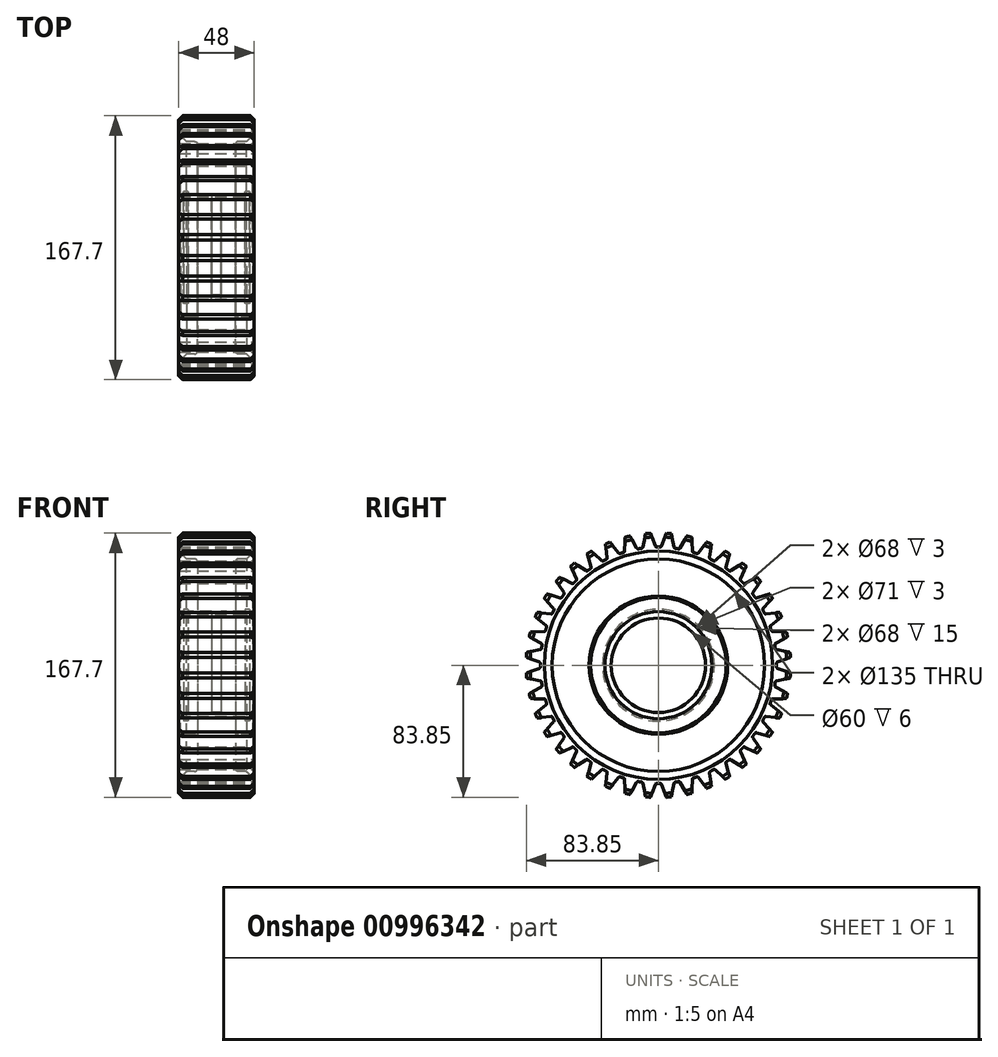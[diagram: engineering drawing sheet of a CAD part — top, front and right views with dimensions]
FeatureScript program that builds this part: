
annotation { "Feature Type Name" : "Feature", "Feature Type Description" : "" }
export const myFeature = defineFeature(function(context is Context, id is Id, definition is map)
    precondition{}
    {
        {
            var Q0;
            Q0=qCreatedBy(makeId("Front.planeOp"),FACE);
            var sketch = newSketch(context, id + "F0", { "sketchPlane" : qUnion([Q0])});
            skLineSegment(sketch, "E0", {"start": v(0, 0) * mm, "end": v(0, 84) * mm, "construction": true});
            skLineSegment(sketch, "E1", {"start": v(0, 84) * mm, "end": v(-24, 84) * mm});
            skLineSegment(sketch, "E2", {"start": v(-24, 84) * mm, "end": v(-24, 67.5) * mm});
            skLineSegment(sketch, "E3", {"start": v(-24, 0) * mm, "end": v(0, 0) * mm, "construction": true});
            skLineSegment(sketch, "E4", {"start": v(-24, 34) * mm, "end": v(-21, 34) * mm});
            skLineSegment(sketch, "E5", {"start": v(-21, 34) * mm, "end": v(-21, 35.5) * mm});
            skLineSegment(sketch, "E6", {"start": v(-21, 35.5) * mm, "end": v(-18, 35.5) * mm});
            skLineSegment(sketch, "E7", {"start": v(-18, 35.5) * mm, "end": v(-18, 34) * mm});
            skLineSegment(sketch, "E8", {"start": v(-18, 34) * mm, "end": v(-3, 34) * mm});
            skLineSegment(sketch, "E9", {"start": v(-3, 34) * mm, "end": v(-3, 30) * mm});
            skLineSegment(sketch, "E10", {"start": v(-3, 30) * mm, "end": v(0, 30) * mm});
            skLineSegment(sketch, "E11", {"start": v(-24, 44) * mm, "end": v(-14, 44) * mm});
            skLineSegment(sketch, "E12", {"start": v(-12, 46) * mm, "end": v(-12, 65.5) * mm});
            skLineSegment(sketch, "E13", {"start": v(-14, 67.5) * mm, "end": v(-24, 67.5) * mm});
            skLineSegment(sketch, "E14.trimOffspring", {"start": v(-24, 44) * mm, "end": v(-24, 34) * mm});
            skPoint(sketch, "E15.visualSharp", {"position": v(-12, 67.5) * mm});
            skArc(sketch, "E15.filletArc", {"start": v(-12, 65.5) * mm, "mid": v(-12.59, 66.91) * mm, "end": v(-14, 67.5) * mm});
            skPoint(sketch, "E16.visualSharp", {"position": v(-12, 44) * mm});
            skArc(sketch, "E16.filletArc", {"start": v(-14, 44) * mm, "mid": v(-12.59, 44.59) * mm, "end": v(-12, 46) * mm});
            skLineSegment(sketch, "E17.MirrorCS", {"start": v(0, 84) * mm, "end": v(24, 84) * mm});
            skLineSegment(sketch, "E18.MirrorCS", {"start": v(24, 84) * mm, "end": v(24, 67.5) * mm});
            skLineSegment(sketch, "E19.MirrorCS", {"start": v(14, 67.5) * mm, "end": v(24, 67.5) * mm});
            skArc(sketch, "E20.MirrorCS", {"start": v(12, 65.5) * mm, "mid": v(12.59, 66.91) * mm, "end": v(14, 67.5) * mm});
            skLineSegment(sketch, "E21.MirrorCS", {"start": v(12, 46) * mm, "end": v(12, 65.5) * mm});
            skArc(sketch, "E22.MirrorCS", {"start": v(14, 44) * mm, "mid": v(12.59, 44.59) * mm, "end": v(12, 46) * mm});
            skLineSegment(sketch, "E23.MirrorCS", {"start": v(24, 44) * mm, "end": v(14, 44) * mm});
            skLineSegment(sketch, "E24.MirrorCS", {"start": v(24, 44) * mm, "end": v(24, 34) * mm});
            skLineSegment(sketch, "E25.MirrorCS", {"start": v(24, 34) * mm, "end": v(21, 34) * mm});
            skLineSegment(sketch, "E26.MirrorCS", {"start": v(21, 34) * mm, "end": v(21, 35.5) * mm});
            skLineSegment(sketch, "E27.MirrorCS", {"start": v(21, 35.5) * mm, "end": v(18, 35.5) * mm});
            skLineSegment(sketch, "E28.MirrorCS", {"start": v(18, 35.5) * mm, "end": v(18, 34) * mm});
            skLineSegment(sketch, "E29.MirrorCS", {"start": v(18, 34) * mm, "end": v(3, 34) * mm});
            skLineSegment(sketch, "E30.MirrorCS", {"start": v(3, 34) * mm, "end": v(3, 30) * mm});
            skLineSegment(sketch, "E31.MirrorCS", {"start": v(3, 30) * mm, "end": v(0, 30) * mm});
            skSolve(sketch);
        }
        {
            var Q0;
            Q0=makeQuery(id+"F0.imprint","IMPRINT",FACE,{"disambiguationData":[TD([[makeQuery(id+"F0.imprint","IMPRINT",EDGE,{"derivedFrom":sQuery(id+"F0.wireOp",EDGE,"E1")}),1.0]])]});
            var Q1;
            Q1=sQuery(id+"F0.wireOp",EDGE,"E3");
            revolve(context, id + "F1", {"surfaceOperationType" : NewSurfaceOperationType.NEW, "entities" : qUnion([Q0]), "axis" : qUnion([Q1]), "revolveType" : RevolveType.FULL});
        }
        {
            var Q0;
            Q0=qCreatedBy(makeId("Right.planeOp"),FACE);
            var sketch = newSketch(context, id + "F2", { "sketchPlane" : qUnion([Q0])});
            skLineSegment(sketch, "E32", {"start": v(0, 0) * mm, "end": v(0, 100.92) * mm, "construction": true});
            skArc(sketch, "E33", {"start": v(1.04, 75) * mm, "mid": v(0, 75) * mm, "end": v(-1.04, 75) * mm});
            skLineSegment(sketch, "E34", {"start": v(2, 75.65) * mm, "end": v(4.98, 83.85) * mm});
            skLineSegment(sketch, "E35.MirrorCS", {"start": v(-2, 75.65) * mm, "end": v(-4.98, 83.85) * mm});
            skPoint(sketch, "E36.visualSharp", {"position": v(-1.75, 74.98) * mm});
            skArc(sketch, "E36.filletArc", {"start": v(-2, 75.65) * mm, "mid": v(-1.62, 75.17) * mm, "end": v(-1.04, 75) * mm});
            skPoint(sketch, "E37.visualSharp", {"position": v(1.75, 74.98) * mm});
            skArc(sketch, "E37.filletArc", {"start": v(1.04, 75) * mm, "mid": v(1.62, 75.17) * mm, "end": v(2, 75.65) * mm});
            skArc(sketch, "E38", {"start": v(-4.98, 83.85) * mm, "mid": v(0, 84) * mm, "end": v(4.98, 83.85) * mm});
            skSolve(sketch);
        }
        {
            var Q0;
            Q0 = qSketchRegion(id + "F2", true);
            extrude(context, id + "F3", {"entities" : qUnion([Q0]), "operationType" : NewBodyOperationType.REMOVE, "endBound" : BoundingType.SYMMETRIC, "oppositeDirection" : true, "depth" : 50 * mm, "offsetDistance" : 25 * mm});
        }
        {
            var Q0;
            Q0=makeQuery(id+"F3.boolean.opBoolean","COPY",FACE,{"derivedFrom":makeQuery(id+"F3.opExtrude","SWEPT_FACE",FACE,{"disambiguationData":[OSD([sQuery(id+"F2.wireOp",EDGE,"E35.MirrorCS")])]})});
            var Q1;
            Q1=makeQuery(id+"F3.boolean.opBoolean","COPY",FACE,{"derivedFrom":makeQuery(id+"F3.opExtrude","SWEPT_FACE",FACE,{"disambiguationData":[OSD([sQuery(id+"F2.wireOp",EDGE,"E36.filletArc")])]})});
            var Q2;
            Q2=makeQuery(id+"F3.boolean.opBoolean","COPY",FACE,{"derivedFrom":makeQuery(id+"F3.opExtrude","SWEPT_FACE",FACE,{"disambiguationData":[OSD([sQuery(id+"F2.wireOp",EDGE,"E33")])]})});
            var Q3;
            Q3=makeQuery(id+"F3.boolean.opBoolean","COPY",FACE,{"derivedFrom":makeQuery(id+"F3.opExtrude","SWEPT_FACE",FACE,{"disambiguationData":[OSD([sQuery(id+"F2.wireOp",EDGE,"E37.filletArc")])]})});
            var Q4;
            Q4=makeQuery(id+"F3.boolean.opBoolean","COPY",FACE,{"derivedFrom":makeQuery(id+"F3.opExtrude","SWEPT_FACE",FACE,{"disambiguationData":[OSD([sQuery(id+"F2.wireOp",EDGE,"E34")])]})});
            var Q5;
            Q5=makeQuery(id+"F1.opRevolve","SWEPT_FACE",FACE,{"disambiguationData":[OSD([sQuery(id+"F0.wireOp",EDGE,"E1"),sQuery(id+"F0.wireOp",EDGE,"E17.MirrorCS")])]});
            circularPattern(context, id + "F4", {"patternType" : PatternType.FACE, "operationType" : NewBodyOperationType.REMOVE, "faces" : qUnion([Q0, Q1, Q2, Q3, Q4]), "axis" : qUnion([Q5]), "angle" : 9 * degree, "instanceCount" : 40});
        }
        {
            var Q0;
            Q0=makeQuery(id+"F1.opRevolve","SWEPT_EDGE",EDGE,{"disambiguationData":[OSD([sQuery(id+"F0.wireOp",EDGE,"E18.MirrorCS"),sQuery(id+"F0.wireOp",EDGE,"E19.MirrorCS")])]});
            var Q1;
            Q1=makeQuery(id+"F1.opRevolve","SWEPT_EDGE",EDGE,{"disambiguationData":[OSD([sQuery(id+"F0.wireOp",EDGE,"E2"),sQuery(id+"F0.wireOp",EDGE,"E13")])]});
            chamfer(context, id + "F5", {"entities" : qUnion([Q0, Q1]), "width" : 5 * mm, "tangentPropagation" : true});
        }
        {
            var Q0;
            Q0=makeQuery(id+"F1.opRevolve","SWEPT_EDGE",EDGE,{"disambiguationData":[OSD([sQuery(id+"F0.wireOp",EDGE,"E11"),sQuery(id+"F0.wireOp",EDGE,"E14.trimOffspring")])]});
            var Q1;
            Q1=makeQuery(id+"F1.opRevolve","SWEPT_EDGE",EDGE,{"disambiguationData":[OSD([sQuery(id+"F0.wireOp",EDGE,"E23.MirrorCS"),sQuery(id+"F0.wireOp",EDGE,"E24.MirrorCS")])]});
            chamfer(context, id + "F6", {"entities" : qUnion([Q0, Q1]), "width" : 1 * mm, "tangentPropagation" : true});
        }
        {
            var Q0;
            Q0=qCreatedBy(makeId("Front.planeOp"),FACE);
            var sketch = newSketch(context, id + "F7", { "sketchPlane" : qUnion([Q0])});
            skLineSegment(sketch, "E39", {"start": v(0, 0) * mm, "end": v(0, 84) * mm, "construction": true});
            skLineSegment(sketch, "E40", {"start": v(0, 84) * mm, "end": v(-24, 84) * mm, "construction": true});
            skLineSegment(sketch, "E41", {"start": v(-24, 84) * mm, "end": v(-24, 67.5) * mm, "construction": true});
            skLineSegment(sketch, "E42", {"start": v(-24, 0) * mm, "end": v(0, 0) * mm, "construction": true});
            skLineSegment(sketch, "E43", {"start": v(-24, 34) * mm, "end": v(-21, 34) * mm, "construction": true});
            skLineSegment(sketch, "E44", {"start": v(-21, 34) * mm, "end": v(-21, 35.5) * mm, "construction": true});
            skLineSegment(sketch, "E45", {"start": v(-21, 35.5) * mm, "end": v(-18, 35.5) * mm, "construction": true});
            skLineSegment(sketch, "E46", {"start": v(-18, 35.5) * mm, "end": v(-18, 34) * mm, "construction": true});
            skLineSegment(sketch, "E47", {"start": v(-18, 34) * mm, "end": v(-3, 34) * mm, "construction": true});
            skLineSegment(sketch, "E48", {"start": v(-3, 34) * mm, "end": v(-3, 30) * mm, "construction": true});
            skLineSegment(sketch, "E49", {"start": v(-3, 30) * mm, "end": v(0, 30) * mm, "construction": true});
            skLineSegment(sketch, "E50", {"start": v(-24, 44) * mm, "end": v(-14, 44) * mm, "construction": true});
            skLineSegment(sketch, "E51", {"start": v(-12, 46) * mm, "end": v(-12, 65.5) * mm, "construction": true});
            skLineSegment(sketch, "E52", {"start": v(-14, 67.5) * mm, "end": v(-24, 67.5) * mm, "construction": true});
            skLineSegment(sketch, "E53.trimOffspring", {"start": v(-24, 44) * mm, "end": v(-24, 34) * mm, "construction": true});
            skPoint(sketch, "E54.visualSharp", {"position": v(-12, 67.5) * mm});
            skArc(sketch, "E54.filletArc", {"start": v(-12, 65.5) * mm, "mid": v(-12.59, 66.91) * mm, "end": v(-14, 67.5) * mm, "construction": true});
            skPoint(sketch, "E55.visualSharp", {"position": v(-12, 44) * mm});
            skArc(sketch, "E55.filletArc", {"start": v(-14, 44) * mm, "mid": v(-12.59, 44.59) * mm, "end": v(-12, 46) * mm, "construction": true});
            skLineSegment(sketch, "E56.MirrorCS", {"start": v(0, 84) * mm, "end": v(24, 84) * mm, "construction": true});
            skLineSegment(sketch, "E57.MirrorCS", {"start": v(24, 84) * mm, "end": v(24, 67.5) * mm, "construction": true});
            skLineSegment(sketch, "E58.MirrorCS", {"start": v(14, 67.5) * mm, "end": v(24, 67.5) * mm, "construction": true});
            skArc(sketch, "E59.MirrorCS", {"start": v(12, 65.5) * mm, "mid": v(12.59, 66.91) * mm, "end": v(14, 67.5) * mm, "construction": true});
            skLineSegment(sketch, "E60.MirrorCS", {"start": v(12, 46) * mm, "end": v(12, 65.5) * mm, "construction": true});
            skArc(sketch, "E61.MirrorCS", {"start": v(14, 44) * mm, "mid": v(12.59, 44.59) * mm, "end": v(12, 46) * mm, "construction": true});
            skLineSegment(sketch, "E62.MirrorCS", {"start": v(24, 44) * mm, "end": v(14, 44) * mm, "construction": true});
            skLineSegment(sketch, "E63.MirrorCS", {"start": v(24, 44) * mm, "end": v(24, 34) * mm, "construction": true});
            skLineSegment(sketch, "E64.MirrorCS", {"start": v(24, 34) * mm, "end": v(21, 34) * mm, "construction": true});
            skLineSegment(sketch, "E65.MirrorCS", {"start": v(21, 34) * mm, "end": v(21, 35.5) * mm, "construction": true});
            skLineSegment(sketch, "E66.MirrorCS", {"start": v(21, 35.5) * mm, "end": v(18, 35.5) * mm, "construction": true});
            skLineSegment(sketch, "E67.MirrorCS", {"start": v(18, 35.5) * mm, "end": v(18, 34) * mm, "construction": true});
            skLineSegment(sketch, "E68.MirrorCS", {"start": v(18, 34) * mm, "end": v(3, 34) * mm, "construction": true});
            skLineSegment(sketch, "E69.MirrorCS", {"start": v(3, 34) * mm, "end": v(3, 30) * mm, "construction": true});
            skLineSegment(sketch, "E70.MirrorCS", {"start": v(3, 30) * mm, "end": v(0, 30) * mm, "construction": true});
            skLineSegment(sketch, "E71", {"start": v(17, 88.5) * mm, "end": v(28.48, 77.01) * mm});
            skLineSegment(sketch, "E72", {"start": v(-17, 88.5) * mm, "end": v(-28.66, 76.84) * mm});
            skLineSegment(sketch, "E73", {"start": v(-17, 88.5) * mm, "end": v(17, 88.5) * mm});
            skLineSegment(sketch, "E74", {"start": v(-28.66, 76.84) * mm, "end": v(-28.66, 104.55) * mm});
            skLineSegment(sketch, "E75", {"start": v(-28.66, 104.55) * mm, "end": v(28.48, 104.55) * mm});
            skLineSegment(sketch, "E76", {"start": v(28.48, 104.55) * mm, "end": v(28.48, 77.01) * mm});
            skSolve(sketch);
        }
        {
            var Q0;
            Q0=makeQuery(id+"F7.imprint","IMPRINT",FACE,{"disambiguationData":[TD([[makeQuery(id+"F7.imprint","IMPRINT",EDGE,{"derivedFrom":sQuery(id+"F7.wireOp",EDGE,"E71")}),1.0]])]});
            var Q1;
            Q1=sQuery(id+"F7.wireOp",EDGE,"E42");
            revolve(context, id + "F8", {"surfaceOperationType" : NewSurfaceOperationType.NEW, "entities" : qUnion([Q0]), "axis" : qUnion([Q1]), "revolveType" : RevolveType.FULL});
        }
        {
            var Q0;
            Q0=makeQuery(id+"F8.opRevolve","SWEPT_BODY",BODY,{"disambiguationData":[OSD([sQuery(id+"F7.wireOp",EDGE,"E71"),sQuery(id+"F7.wireOp",EDGE,"E72"),sQuery(id+"F7.wireOp",EDGE,"E73"),sQuery(id+"F7.wireOp",EDGE,"E74"),sQuery(id+"F7.wireOp",EDGE,"E75"),sQuery(id+"F7.wireOp",EDGE,"E76")])]});
            var Q1;
            Q1=makeQuery(id+"F1.opRevolve","SWEPT_BODY",BODY,{"disambiguationData":[OSD([sQuery(id+"F0.wireOp",EDGE,"E1"),sQuery(id+"F0.wireOp",EDGE,"E2"),sQuery(id+"F0.wireOp",EDGE,"E4"),sQuery(id+"F0.wireOp",EDGE,"E5"),sQuery(id+"F0.wireOp",EDGE,"E6"),sQuery(id+"F0.wireOp",EDGE,"E7"),sQuery(id+"F0.wireOp",EDGE,"E8"),sQuery(id+"F0.wireOp",EDGE,"E9"),sQuery(id+"F0.wireOp",EDGE,"E10"),sQuery(id+"F0.wireOp",EDGE,"E11"),sQuery(id+"F0.wireOp",EDGE,"E12"),sQuery(id+"F0.wireOp",EDGE,"E13"),sQuery(id+"F0.wireOp",EDGE,"E14.trimOffspring"),sQuery(id+"F0.wireOp",EDGE,"E15.filletArc"),sQuery(id+"F0.wireOp",EDGE,"E16.filletArc"),sQuery(id+"F0.wireOp",EDGE,"E17.MirrorCS"),sQuery(id+"F0.wireOp",EDGE,"E18.MirrorCS"),sQuery(id+"F0.wireOp",EDGE,"E19.MirrorCS"),sQuery(id+"F0.wireOp",EDGE,"E20.MirrorCS"),sQuery(id+"F0.wireOp",EDGE,"E21.MirrorCS"),sQuery(id+"F0.wireOp",EDGE,"E22.MirrorCS"),sQuery(id+"F0.wireOp",EDGE,"E23.MirrorCS"),sQuery(id+"F0.wireOp",EDGE,"E24.MirrorCS"),sQuery(id+"F0.wireOp",EDGE,"E25.MirrorCS"),sQuery(id+"F0.wireOp",EDGE,"E26.MirrorCS"),sQuery(id+"F0.wireOp",EDGE,"E27.MirrorCS"),sQuery(id+"F0.wireOp",EDGE,"E28.MirrorCS"),sQuery(id+"F0.wireOp",EDGE,"E29.MirrorCS"),sQuery(id+"F0.wireOp",EDGE,"E30.MirrorCS"),sQuery(id+"F0.wireOp",EDGE,"E31.MirrorCS")])]});
            booleanBodies(context, id + "F9", {"operationType" : BooleanOperationType.SUBTRACTION, "tools" : qUnion([Q0]), "targets" : qUnion([Q1])});
        }
    });
